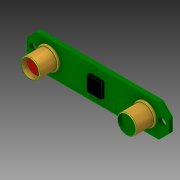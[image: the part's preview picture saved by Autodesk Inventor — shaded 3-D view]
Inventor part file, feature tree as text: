
AUTODESK INVENTOR PART (.ipt)
format: ipt  version: 2016 SP1 (Build 200210100, 210)  size: 807,424 bytes
history: native  units: in
note: dims shown in document units (in); Inventor stores cm internally (conversion verified against a paired STEP export)
features: other x4, sketch x4, extrude x3, fillet x3, mirror x3, plane x2, revolve x1
ambient origin geometry x8: Origin, YZ Plane, XZ Plane, XY Plane, X Axis, Y Axis, Z Axis, Center Point
bodies: Solid1 (feature_tree), Solid2 (feature_tree)
feature tree (20):
  other  "ZX_Distance_and_Gesture_Sensor_v10.brd_Outline"
  sketch  "Sketch2"  dims[d20=0.3in d21=0.0in d22=0.3in d23=0.015in d24=0.2375in d25=0.0in]
  extrude  "Extrusion2"  Depth=0.063in
  extrude  "Extrusion3"  Depth=0.3in
  fillet  "Fillet1"  Radius=0.015in
  fillet  "Fillet2"  Radius=0.2375in
  plane  "Work Plane1"
  revolve  "Revolution1"  [1 undecoded]
  plane  "Work Plane2"
  mirror  "Mirror1"
  mirror  "Mirror2"
  mirror  "Mirror3"
  extrude  "Extrusion4"  TaperAngle=90.0deg  [1 undecoded]
  sketch  "Sketch5"  dims[d28=90.0deg d29=90.0deg d30=0.05in d31=0.0in d38=0.01in]
  fillet  "Fillet3"  Radius=0.05in
  sketch  "Sketch1"  dims[d0=0.063in d1=0.0in d5=2.25in]
  other  "Image1"
  other  "Work Axis1"
  sketch  "Sketch4"  dims[d26=0.01in d27=0.05in]
  other  "Image2"
note: 2 required parameter values undecoded (feature->parameter linkage not recoverable at this tier; creation-order binding heuristic only, values carry confidence <= 0.55)